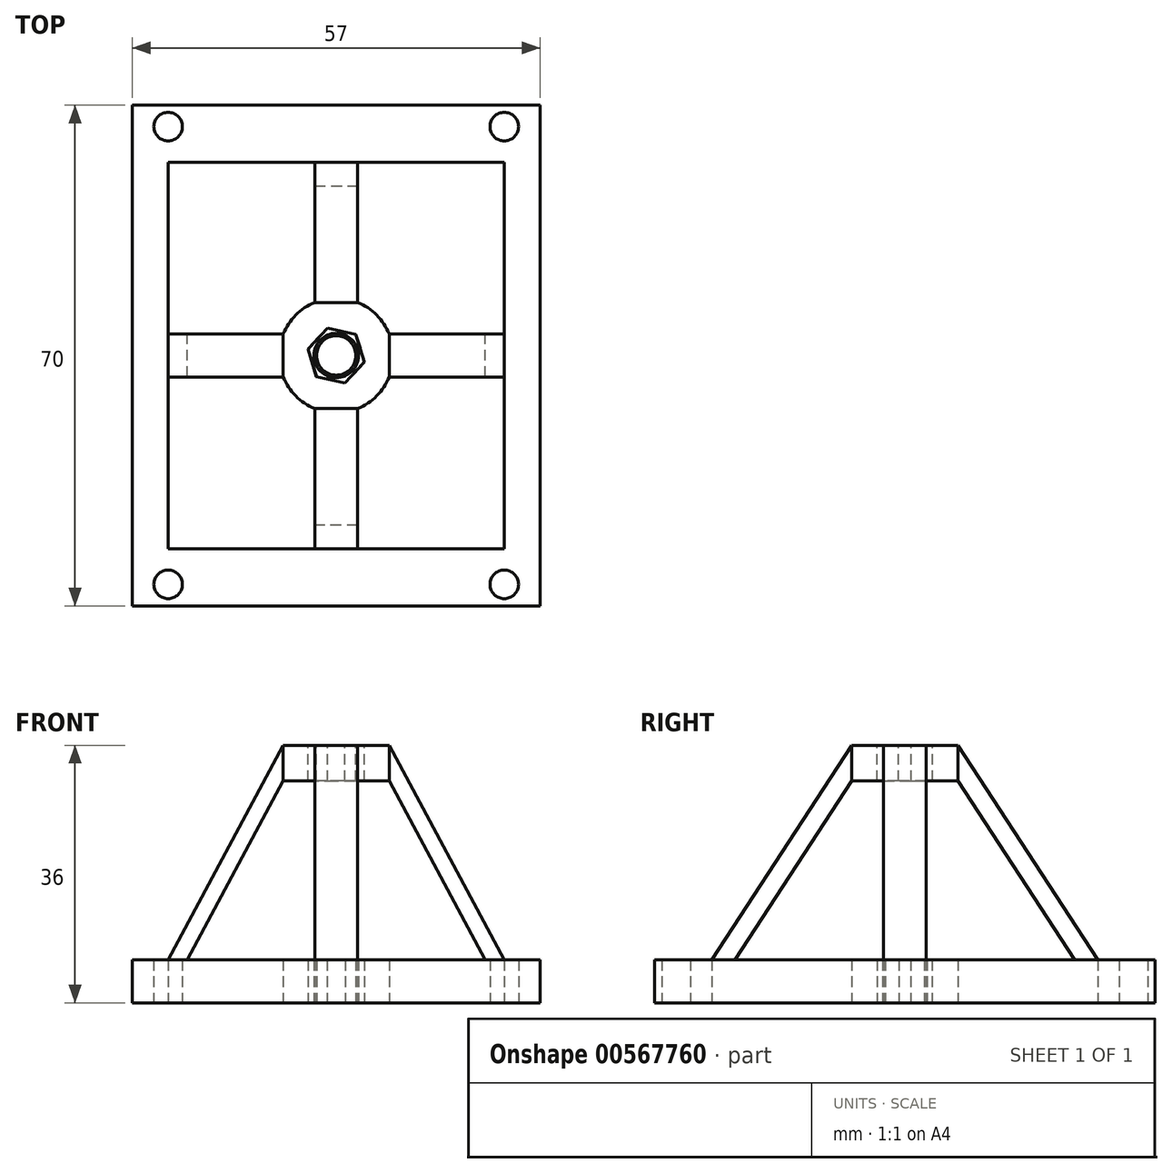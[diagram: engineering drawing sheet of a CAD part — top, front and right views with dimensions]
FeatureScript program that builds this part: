
annotation { "Feature Type Name" : "Feature", "Feature Type Description" : "" }
export const myFeature = defineFeature(function(context is Context, id is Id, definition is map)
    precondition{}
    {
        {
            var Q0;
            Q0=qCreatedBy(makeId("Top.planeOp"),FACE);
            var sketch = newSketch(context, id + "F0", { "sketchPlane" : qUnion([Q0])});
            skLineSegment(sketch, "E0.bottom", {"start": v(28.5, 35) * mm, "end": v(-28.5, 35) * mm});
            skLineSegment(sketch, "E0.top", {"start": v(28.5, -35) * mm, "end": v(-28.5, -35) * mm});
            skLineSegment(sketch, "E0.left", {"start": v(28.5, 35) * mm, "end": v(28.5, -35) * mm});
            skLineSegment(sketch, "E0.right", {"start": v(-28.5, 35) * mm, "end": v(-28.5, -35) * mm});
            skPoint(sketch, "E0.middle", {"position": v(0, 0) * mm});
            skCircle(sketch, "E1", {"center": v(-23.5, -32) * mm, "radius": 2 * mm});
            skCircle(sketch, "E2", {"center": v(-23.5, 32) * mm, "radius": 2 * mm});
            skCircle(sketch, "E3", {"center": v(23.5, 32) * mm, "radius": 2 * mm});
            skCircle(sketch, "E4", {"center": v(23.5, -32) * mm, "radius": 2 * mm});
            skCircle(sketch, "E5.cCircle", {"center": v(0, 0) * mm, "radius": 3.5 * mm, "construction": true});
            skLineSegment(sketch, "E5.0", {"start": v(-3.95, 0.85) * mm, "end": v(-1.24, 3.85) * mm});
            skLineSegment(sketch, "E5.1", {"start": v(-1.24, 3.85) * mm, "end": v(2.7, 3) * mm});
            skLineSegment(sketch, "E5.2", {"start": v(2.7, 3) * mm, "end": v(3.95, -0.85) * mm});
            skLineSegment(sketch, "E5.3", {"start": v(3.95, -0.85) * mm, "end": v(1.24, -3.85) * mm});
            skLineSegment(sketch, "E5.4", {"start": v(1.24, -3.85) * mm, "end": v(-2.7, -3) * mm});
            skLineSegment(sketch, "E5.5", {"start": v(-2.7, -3) * mm, "end": v(-3.95, 0.85) * mm});
            skPoint(sketch, "E5.0.midPoint", {"position": v(-2.6, 2.35) * mm});
            skLineSegment(sketch, "E6.bottom", {"start": v(-23.5, -27) * mm, "end": v(-3, -27) * mm});
            skLineSegment(sketch, "E6.top", {"start": v(-23.5, 27) * mm, "end": v(-3, 27) * mm});
            skLineSegment(sketch, "E6.left", {"start": v(-23.5, -27) * mm, "end": v(-23.5, -3) * mm});
            skLineSegment(sketch, "E6.right", {"start": v(23.5, -27) * mm, "end": v(23.5, -3) * mm});
            skArc(sketch, "E7", {"start": v(7.42, 3) * mm, "mid": v(5.66, 5.66) * mm, "end": v(3, 7.42) * mm});
            skLineSegment(sketch, "E8.left", {"start": v(3, -27) * mm, "end": v(3, -7.42) * mm});
            skLineSegment(sketch, "E8.right", {"start": v(-3, -27) * mm, "end": v(-3, -7.42) * mm});
            skLineSegment(sketch, "E9.bottom", {"start": v(-23.5, -3) * mm, "end": v(-7.42, -3) * mm});
            skLineSegment(sketch, "E9.top", {"start": v(-23.5, 3) * mm, "end": v(-7.42, 3) * mm});
            skPoint(sketch, "E9.middle", {"position": v(-0.2, 0) * mm});
            skLineSegment(sketch, "E10.trimOffspring", {"start": v(7.42, -3) * mm, "end": v(23.5, -3) * mm});
            skLineSegment(sketch, "E11.trimOffspring", {"start": v(3, -1.9) * mm, "end": v(3, -1.8) * mm});
            skLineSegment(sketch, "E12.trimOffspring", {"start": v(3, 1.8) * mm, "end": v(3, 3) * mm});
            skLineSegment(sketch, "E13.trimOffspring", {"start": v(3, 7.42) * mm, "end": v(3, 27) * mm});
            skLineSegment(sketch, "E14.trimOffspring", {"start": v(7.42, 3) * mm, "end": v(23.5, 3) * mm});
            skLineSegment(sketch, "E15.trimOffspring", {"start": v(23.5, 3) * mm, "end": v(23.5, 27) * mm});
            skPoint(sketch, "E16.orphan", {"position": v(25.8, -3) * mm});
            skPoint(sketch, "E17.orphan", {"position": v(25.8, 3) * mm});
            skPoint(sketch, "E18.orphan", {"position": v(-26.2, -3) * mm});
            skPoint(sketch, "E19.orphan", {"position": v(-26.2, 3) * mm});
            skLineSegment(sketch, "E20.trimOffspring", {"start": v(-23.5, 3) * mm, "end": v(-23.5, 27) * mm});
            skArc(sketch, "E21.trimOffspring", {"start": v(-7.42, -3) * mm, "mid": v(-5.66, -5.66) * mm, "end": v(-3, -7.42) * mm});
            skArc(sketch, "E22.trimOffspring", {"start": v(3, -7.42) * mm, "mid": v(5.66, -5.66) * mm, "end": v(7.42, -3) * mm});
            skArc(sketch, "E23.trimOffspring", {"start": v(-3, 7.42) * mm, "mid": v(-5.66, 5.66) * mm, "end": v(-7.42, 3) * mm});
            skLineSegment(sketch, "E24.trimOffspring", {"start": v(-3, 7.42) * mm, "end": v(-3, 27) * mm});
            skLineSegment(sketch, "E25.trimOffspring", {"start": v(3, 27) * mm, "end": v(23.5, 27) * mm});
            skLineSegment(sketch, "E26.trimOffspring", {"start": v(3, -27) * mm, "end": v(23.5, -27) * mm});
            skCircle(sketch, "E27", {"center": v(0, 0) * mm, "radius": 3.11 * mm});
            skCircle(sketch, "E28", {"center": v(0, 0) * mm, "radius": 2.75 * mm});
            skSolve(sketch);
        }
        {
            var Q0;
            Q0=makeQuery(id+"F0.imprint","IMPRINT",FACE,{"disambiguationData":[TD([[makeQuery(id+"F0.imprint","IMPRINT",EDGE,{"derivedFrom":sQuery(id+"F0.wireOp",EDGE,"E0.bottom")}),1.0]])]});
            var Q1;
            Q1=makeQuery(id+"F0.imprint","IMPRINT",FACE,{"disambiguationData":[TD([[makeQuery(id+"F0.imprint","IMPRINT",EDGE,{"derivedFrom":sQuery(id+"F0.wireOp",EDGE,"E27")}),1.0]])]});
            extrude(context, id + "F1", {"entities" : qUnion([Q0, Q1]), "depth" : 6 * mm, "offsetDistance" : 25 * mm});
        }
        {
            var Q0;
            Q0=makeQuery(id+"F1.opExtrude","CAP_FACE",FACE,{"disambiguationData":[OSD([sQuery(id+"F0.wireOp",EDGE,"E0.bottom"),sQuery(id+"F0.wireOp",EDGE,"E0.top"),sQuery(id+"F0.wireOp",EDGE,"E0.left"),sQuery(id+"F0.wireOp",EDGE,"E0.right"),sQuery(id+"F0.wireOp",EDGE,"E1"),sQuery(id+"F0.wireOp",EDGE,"E2"),sQuery(id+"F0.wireOp",EDGE,"E3"),sQuery(id+"F0.wireOp",EDGE,"E4"),sQuery(id+"F0.wireOp",EDGE,"E5.0"),sQuery(id+"F0.wireOp",EDGE,"E5.1"),sQuery(id+"F0.wireOp",EDGE,"E5.2"),sQuery(id+"F0.wireOp",EDGE,"E5.3"),sQuery(id+"F0.wireOp",EDGE,"E5.4"),sQuery(id+"F0.wireOp",EDGE,"E5.5"),sQuery(id+"F0.wireOp",EDGE,"E6.bottom"),sQuery(id+"F0.wireOp",EDGE,"E6.top"),sQuery(id+"F0.wireOp",EDGE,"E6.left"),sQuery(id+"F0.wireOp",EDGE,"E6.right"),sQuery(id+"F0.wireOp",EDGE,"E7"),sQuery(id+"F0.wireOp",EDGE,"E8.left"),sQuery(id+"F0.wireOp",EDGE,"E8.right"),sQuery(id+"F0.wireOp",EDGE,"E9.bottom"),sQuery(id+"F0.wireOp",EDGE,"E9.top"),sQuery(id+"F0.wireOp",EDGE,"E10.trimOffspring"),sQuery(id+"F0.wireOp",EDGE,"E13.trimOffspring"),sQuery(id+"F0.wireOp",EDGE,"E14.trimOffspring"),sQuery(id+"F0.wireOp",EDGE,"E15.trimOffspring"),sQuery(id+"F0.wireOp",EDGE,"E20.trimOffspring"),sQuery(id+"F0.wireOp",EDGE,"E21.trimOffspring"),sQuery(id+"F0.wireOp",EDGE,"E22.trimOffspring"),sQuery(id+"F0.wireOp",EDGE,"E23.trimOffspring"),sQuery(id+"F0.wireOp",EDGE,"E24.trimOffspring"),sQuery(id+"F0.wireOp",EDGE,"E25.trimOffspring"),sQuery(id+"F0.wireOp",EDGE,"E26.trimOffspring")])],"isStart":false});
            var sketch = newSketch(context, id + "F2", { "sketchPlane" : qUnion([Q0])});
            skLineSegment(sketch, "E29.bottom", {"start": v(-3, 27) * mm, "end": v(3, 27) * mm});
            skLineSegment(sketch, "E29.top", {"start": v(-3, -27) * mm, "end": v(3, -27) * mm});
            skLineSegment(sketch, "E29.left", {"start": v(-3, 27) * mm, "end": v(-3, 4) * mm});
            skLineSegment(sketch, "E29.right", {"start": v(3, 27) * mm, "end": v(3, 4) * mm});
            skPoint(sketch, "E29.middle", {"position": v(0, 0) * mm});
            skLineSegment(sketch, "E30.bottom", {"start": v(-23.5, -3) * mm, "end": v(-4, -3) * mm});
            skLineSegment(sketch, "E30.top", {"start": v(-23.5, 3) * mm, "end": v(-4, 3) * mm});
            skLineSegment(sketch, "E30.left", {"start": v(-23.5, -3) * mm, "end": v(-23.5, 3) * mm});
            skLineSegment(sketch, "E30.right", {"start": v(23.5, -3) * mm, "end": v(23.5, 3) * mm});
            skCircle(sketch, "E31", {"center": v(0, 0) * mm, "radius": 5 * mm});
            skLineSegment(sketch, "E32.trimOffspring", {"start": v(4, -3) * mm, "end": v(23.5, -3) * mm});
            skLineSegment(sketch, "E33.trimOffspring", {"start": v(3, -4) * mm, "end": v(3, -27) * mm});
            skLineSegment(sketch, "E34.trimOffspring", {"start": v(4, 3) * mm, "end": v(23.5, 3) * mm});
            skLineSegment(sketch, "E35.trimOffspring", {"start": v(-3, -4) * mm, "end": v(-3, -27) * mm});
            skSolve(sketch);
        }
        {
            var Q0;
            {var subQ4=sQuery(id+"F2.wireOp",EDGE,"E29.top");Q0=makeQuery(id+"F2.imprint","IMPRINT",FACE,{"disambiguationData":[TD([[makeQuery(id+"F2.imprint","IMPRINT",EDGE,{"derivedFrom":subQ4}),1.0]])]});}
            var Q1;
            {var subQ6=sQuery(id+"F2.wireOp",EDGE,"E30.right");Q1=makeQuery(id+"F2.imprint","IMPRINT",FACE,{"disambiguationData":[TD([[makeQuery(id+"F2.imprint","IMPRINT",EDGE,{"derivedFrom":subQ6}),1.0]])]});}
            var Q2;
            {var subQ5=sQuery(id+"F2.wireOp",EDGE,"E29.bottom");Q2=makeQuery(id+"F2.imprint","IMPRINT",FACE,{"disambiguationData":[TD([[makeQuery(id+"F2.imprint","IMPRINT",EDGE,{"derivedFrom":subQ5}),-1.0]])]});}
            var Q3;
            {var subQ4=sQuery(id+"F2.wireOp",EDGE,"E30.left");Q3=makeQuery(id+"F2.imprint","IMPRINT",FACE,{"disambiguationData":[TD([[makeQuery(id+"F2.imprint","IMPRINT",EDGE,{"derivedFrom":subQ4}),-1.0]])]});}
            extrude(context, id + "F3", {"entities" : qUnion([Q0, Q1, Q2, Q3]), "operationType" : NewBodyOperationType.ADD, "depth" : 30 * mm, "offsetDistance" : 25 * mm});
        }
        {
            var Q0;
            Q0=makeQuery(id+"F3.opExtrude","CAP_FACE",FACE,{"disambiguationData":[OSD([sQuery(id+"F2.wireOp",EDGE,"E30.bottom"),sQuery(id+"F2.wireOp",EDGE,"E30.top"),sQuery(id+"F2.wireOp",EDGE,"E30.left"),sQuery(id+"F2.wireOp",EDGE,"E31")])],"isStart":false});
            var sketch = newSketch(context, id + "F4", { "sketchPlane" : qUnion([Q0])});
            skCircle(sketch, "E36", {"center": v(0, 0) * mm, "radius": 8 * mm});
            skCircle(sketch, "E37.cCircle", {"center": v(0, 0) * mm, "radius": 3.5 * mm, "construction": true});
            skLineSegment(sketch, "E37.0", {"start": v(-3.94, 0.92) * mm, "end": v(-1.18, 3.87) * mm});
            skLineSegment(sketch, "E37.1", {"start": v(-1.18, 3.87) * mm, "end": v(2.76, 2.95) * mm});
            skLineSegment(sketch, "E37.2", {"start": v(2.76, 2.95) * mm, "end": v(3.94, -0.92) * mm});
            skLineSegment(sketch, "E37.3", {"start": v(3.94, -0.92) * mm, "end": v(1.18, -3.87) * mm});
            skLineSegment(sketch, "E37.4", {"start": v(1.18, -3.87) * mm, "end": v(-2.76, -2.95) * mm});
            skLineSegment(sketch, "E37.5", {"start": v(-2.76, -2.95) * mm, "end": v(-3.94, 0.92) * mm});
            skPoint(sketch, "E37.0.midPoint", {"position": v(-2.56, 2.4) * mm});
            skSolve(sketch);
        }
        {
            var Q0;
            Q0=makeQuery(id+"F4.imprint","IMPRINT",FACE,{"disambiguationData":[TD([[makeQuery(id+"F4.imprint","IMPRINT",EDGE,{"derivedFrom":sQuery(id+"F4.wireOp",EDGE,"E37.0")}),1.0]])]});
            var Q1;
            {var subQ1=sQuery(id+"F2.wireOp",EDGE,"E30.bottom");var subQ7=sQuery(id+"F2.wireOp",EDGE,"E31");var subQ8=makeQuery(id+"F3.opExtrude","CAP_EDGE",EDGE,{"disambiguationData":[OSD([subQ7]),TDD([makeQuery(id+"F2.imprint","IMPRINT",EDGE,{"disambiguationData":[TD([[makeQuery(id+"F2.imprint","INTERSECT",VERTEX,{"derivedFrom":[subQ1,subQ7]}),1.0]])],"derivedFrom":subQ7})])],"isStart":false});Q1=makeQuery(id+"F4.imprint","IMPRINT",FACE,{"disambiguationData":[TD([[makeQuery(id+"F4.imprint","IMPRINT",EDGE,{"derivedFrom":subQ8}),-1.0]])]});}
            extrude(context, id + "F5", {"entities" : qUnion([Q0, Q1]), "operationType" : NewBodyOperationType.ADD, "oppositeDirection" : true, "depth" : 5 * mm, "offsetDistance" : 25 * mm});
        }
        {
            var Q0;
            Q0=makeQuery(id+"F3.boolean.opBoolean","MERGE",FACE,{"derivedFrom":[makeQuery(id+"F1.opExtrude","SWEPT_FACE",FACE,{"disambiguationData":[OSD([sQuery(id+"F0.wireOp",EDGE,"E8.left")])]}),makeQuery(id+"F3.opExtrude","SWEPT_FACE",FACE,{"disambiguationData":[OSD([sQuery(id+"F2.wireOp",EDGE,"E33.trimOffspring")])]})]});
            var sketch = newSketch(context, id + "F6", { "sketchPlane" : qUnion([Q0])});
            skLineSegment(sketch, "E38", {"start": v(-7.42, 36) * mm, "end": v(-27, 6) * mm});
            skLineSegment(sketch, "E39", {"start": v(-27, 6) * mm, "end": v(-27, 36) * mm});
            skLineSegment(sketch, "E40", {"start": v(-27, 36) * mm, "end": v(-7.42, 36) * mm});
            skSolve(sketch);
        }
        {
            var Q0;
            Q0=makeQuery(id+"F6.imprint","IMPRINT",FACE,{"disambiguationData":[TD([[makeQuery(id+"F6.imprint","IMPRINT",EDGE,{"derivedFrom":sQuery(id+"F6.wireOp",EDGE,"E38")}),-1.0]])]});
            extrude(context, id + "F7", {"entities" : qUnion([Q0]), "operationType" : NewBodyOperationType.REMOVE, "oppositeDirection" : true, "depth" : 25 * mm, "offsetDistance" : 25 * mm});
        }
        {
            var Q0;
            Q0=makeQuery(id+"F3.boolean.opBoolean","MERGE",FACE,{"derivedFrom":[makeQuery(id+"F1.opExtrude","SWEPT_FACE",FACE,{"disambiguationData":[OSD([sQuery(id+"F0.wireOp",EDGE,"E9.top")])]}),makeQuery(id+"F3.opExtrude","SWEPT_FACE",FACE,{"disambiguationData":[OSD([sQuery(id+"F2.wireOp",EDGE,"E30.top")])]})]});
            var sketch = newSketch(context, id + "F8", { "sketchPlane" : qUnion([Q0])});
            skLineSegment(sketch, "E41", {"start": v(7.42, 36) * mm, "end": v(23.5, 6) * mm});
            skLineSegment(sketch, "E42", {"start": v(23.5, 6) * mm, "end": v(23.5, 36) * mm});
            skLineSegment(sketch, "E43", {"start": v(23.5, 36) * mm, "end": v(7.42, 36) * mm});
            skSolve(sketch);
        }
        {
            var Q0;
            Q0=makeQuery(id+"F8.imprint","IMPRINT",FACE,{"disambiguationData":[TD([[makeQuery(id+"F8.imprint","IMPRINT",EDGE,{"derivedFrom":sQuery(id+"F8.wireOp",EDGE,"E41")}),1.0]])]});
            extrude(context, id + "F9", {"entities" : qUnion([Q0]), "operationType" : NewBodyOperationType.REMOVE, "oppositeDirection" : true, "depth" : 25 * mm, "offsetDistance" : 25 * mm});
        }
        {
            var Q0;
            Q0=makeQuery(id+"F3.boolean.opBoolean","MERGE",FACE,{"derivedFrom":[makeQuery(id+"F1.opExtrude","SWEPT_FACE",FACE,{"disambiguationData":[OSD([sQuery(id+"F0.wireOp",EDGE,"E24.trimOffspring")])]}),makeQuery(id+"F3.opExtrude","SWEPT_FACE",FACE,{"disambiguationData":[OSD([sQuery(id+"F2.wireOp",EDGE,"E29.left")])]})]});
            var sketch = newSketch(context, id + "F10", { "sketchPlane" : qUnion([Q0])});
            skLineSegment(sketch, "E44", {"start": v(-7.42, 36) * mm, "end": v(-27, 6) * mm});
            skLineSegment(sketch, "E45", {"start": v(-27, 6) * mm, "end": v(-27, 36) * mm});
            skLineSegment(sketch, "E46", {"start": v(-27, 36) * mm, "end": v(-7.42, 36) * mm});
            skSolve(sketch);
        }
        {
            var Q0;
            Q0=makeQuery(id+"F10.imprint","IMPRINT",FACE,{"disambiguationData":[TD([[makeQuery(id+"F10.imprint","IMPRINT",EDGE,{"derivedFrom":sQuery(id+"F10.wireOp",EDGE,"E44")}),-1.0]])]});
            extrude(context, id + "F11", {"entities" : qUnion([Q0]), "operationType" : NewBodyOperationType.REMOVE, "oppositeDirection" : true, "depth" : 25 * mm, "offsetDistance" : 25 * mm});
        }
        {
            var Q0;
            Q0=makeQuery(id+"F3.boolean.opBoolean","MERGE",FACE,{"derivedFrom":[makeQuery(id+"F1.opExtrude","SWEPT_FACE",FACE,{"disambiguationData":[OSD([sQuery(id+"F0.wireOp",EDGE,"E14.trimOffspring")])]}),makeQuery(id+"F3.opExtrude","SWEPT_FACE",FACE,{"disambiguationData":[OSD([sQuery(id+"F2.wireOp",EDGE,"E34.trimOffspring")])]})]});
            var sketch = newSketch(context, id + "F12", { "sketchPlane" : qUnion([Q0])});
            skLineSegment(sketch, "E47", {"start": v(-7.42, 36) * mm, "end": v(-23.5, 6) * mm});
            skLineSegment(sketch, "E48", {"start": v(-23.5, 6) * mm, "end": v(-23.5, 36) * mm});
            skLineSegment(sketch, "E49", {"start": v(-23.5, 36) * mm, "end": v(-7.42, 36) * mm});
            skSolve(sketch);
        }
        {
            var Q0;
            Q0=makeQuery(id+"F12.imprint","IMPRINT",FACE,{"disambiguationData":[TD([[makeQuery(id+"F12.imprint","IMPRINT",EDGE,{"derivedFrom":sQuery(id+"F12.wireOp",EDGE,"E47")}),-1.0]])]});
            extrude(context, id + "F13", {"entities" : qUnion([Q0]), "operationType" : NewBodyOperationType.REMOVE, "oppositeDirection" : true, "depth" : 25 * mm, "offsetDistance" : 25 * mm});
        }
        {
            var Q0;
            Q0=makeQuery(id+"F3.boolean.opBoolean","MERGE",FACE,{"derivedFrom":[makeQuery(id+"F1.opExtrude","SWEPT_FACE",FACE,{"disambiguationData":[OSD([sQuery(id+"F0.wireOp",EDGE,"E13.trimOffspring")])]}),makeQuery(id+"F3.opExtrude","SWEPT_FACE",FACE,{"disambiguationData":[OSD([sQuery(id+"F2.wireOp",EDGE,"E29.right")])]})]});
            var sketch = newSketch(context, id + "F14", { "sketchPlane" : qUnion([Q0])});
            skLineSegment(sketch, "E50", {"start": v(4, 6) * mm, "end": v(23.74, 6) * mm});
            skLineSegment(sketch, "E51", {"start": v(23.74, 6) * mm, "end": v(7.42, 31) * mm});
            skLineSegment(sketch, "E52", {"start": v(7.42, 31) * mm, "end": v(4, 31) * mm});
            skLineSegment(sketch, "E53", {"start": v(4, 31) * mm, "end": v(4, 6) * mm});
            skSolve(sketch);
        }
        {
            var Q0;
            {var subQ0=sQuery(id+"F14.wireOp",EDGE,"E51");Q0=makeQuery(id+"F14.imprint","IMPRINT",FACE,{"disambiguationData":[TD([[makeQuery(id+"F14.imprint","IMPRINT",EDGE,{"derivedFrom":subQ0}),1.0]])]});}
            extrude(context, id + "F15", {"entities" : qUnion([Q0]), "operationType" : NewBodyOperationType.REMOVE, "oppositeDirection" : true, "depth" : 25 * mm, "offsetDistance" : 25 * mm});
        }
        {
            var Q0;
            Q0=makeQuery(id+"F3.boolean.opBoolean","MERGE",FACE,{"derivedFrom":[makeQuery(id+"F1.opExtrude","SWEPT_FACE",FACE,{"disambiguationData":[OSD([sQuery(id+"F0.wireOp",EDGE,"E9.top")])]}),makeQuery(id+"F3.opExtrude","SWEPT_FACE",FACE,{"disambiguationData":[OSD([sQuery(id+"F2.wireOp",EDGE,"E30.top")])]})]});
            var sketch = newSketch(context, id + "F16", { "sketchPlane" : qUnion([Q0])});
            skLineSegment(sketch, "E54", {"start": v(4, 6) * mm, "end": v(20.82, 6) * mm});
            skLineSegment(sketch, "E55", {"start": v(20.82, 6) * mm, "end": v(7.42, 31) * mm});
            skLineSegment(sketch, "E56", {"start": v(7.42, 31) * mm, "end": v(4, 31) * mm});
            skLineSegment(sketch, "E57", {"start": v(4, 31) * mm, "end": v(4, 6) * mm});
            skSolve(sketch);
        }
        {
            var Q0;
            {var subQ0=sQuery(id+"F16.wireOp",EDGE,"E55");Q0=makeQuery(id+"F16.imprint","IMPRINT",FACE,{"disambiguationData":[TD([[makeQuery(id+"F16.imprint","IMPRINT",EDGE,{"derivedFrom":subQ0}),1.0]])]});}
            extrude(context, id + "F17", {"entities" : qUnion([Q0]), "operationType" : NewBodyOperationType.REMOVE, "oppositeDirection" : true, "depth" : 25 * mm, "offsetDistance" : 25 * mm});
        }
        {
            var Q0;
            Q0=makeQuery(id+"F3.boolean.opBoolean","MERGE",FACE,{"derivedFrom":[makeQuery(id+"F1.opExtrude","SWEPT_FACE",FACE,{"disambiguationData":[OSD([sQuery(id+"F0.wireOp",EDGE,"E8.right")])]}),makeQuery(id+"F3.opExtrude","SWEPT_FACE",FACE,{"disambiguationData":[OSD([sQuery(id+"F2.wireOp",EDGE,"E35.trimOffspring")])]})]});
            var sketch = newSketch(context, id + "F18", { "sketchPlane" : qUnion([Q0])});
            skLineSegment(sketch, "E58", {"start": v(4, 6) * mm, "end": v(23.74, 6) * mm});
            skLineSegment(sketch, "E59", {"start": v(23.74, 6) * mm, "end": v(7.42, 31) * mm});
            skLineSegment(sketch, "E60", {"start": v(7.42, 31) * mm, "end": v(4, 31) * mm});
            skLineSegment(sketch, "E61", {"start": v(4, 31) * mm, "end": v(4, 6) * mm});
            skSolve(sketch);
        }
        {
            var Q0;
            Q0 = qSketchRegion(id + "F18", true);
            extrude(context, id + "F19", {"entities" : qUnion([Q0]), "operationType" : NewBodyOperationType.REMOVE, "oppositeDirection" : true, "depth" : 25 * mm, "offsetDistance" : 25 * mm});
        }
        {
            var Q0;
            Q0=makeQuery(id+"F3.boolean.opBoolean","MERGE",FACE,{"derivedFrom":[makeQuery(id+"F1.opExtrude","SWEPT_FACE",FACE,{"disambiguationData":[OSD([sQuery(id+"F0.wireOp",EDGE,"E14.trimOffspring")])]}),makeQuery(id+"F3.opExtrude","SWEPT_FACE",FACE,{"disambiguationData":[OSD([sQuery(id+"F2.wireOp",EDGE,"E34.trimOffspring")])]})]});
            var sketch = newSketch(context, id + "F20", { "sketchPlane" : qUnion([Q0])});
            skLineSegment(sketch, "E62", {"start": v(-4, 6) * mm, "end": v(-20.82, 6) * mm});
            skPoint(sketch, "E62.endSnap0", {"position": v(-5.7, 6) * mm});
            skLineSegment(sketch, "E63", {"start": v(-20.82, 6) * mm, "end": v(-7.42, 31) * mm});
            skLineSegment(sketch, "E64", {"start": v(-7.42, 31) * mm, "end": v(-4, 31) * mm});
            skLineSegment(sketch, "E65", {"start": v(-4, 31) * mm, "end": v(-4, 6) * mm});
            skLineSegment(sketch, "E66", {"start": v(-5.7, 6) * mm, "end": v(-4, 6) * mm});
            skSolve(sketch);
        }
        {
            var Q0;
            Q0 = qSketchRegion(id + "F20", true);
            extrude(context, id + "F21", {"entities" : qUnion([Q0]), "operationType" : NewBodyOperationType.REMOVE, "oppositeDirection" : true, "depth" : 25 * mm, "offsetDistance" : 25 * mm});
        }
    });
